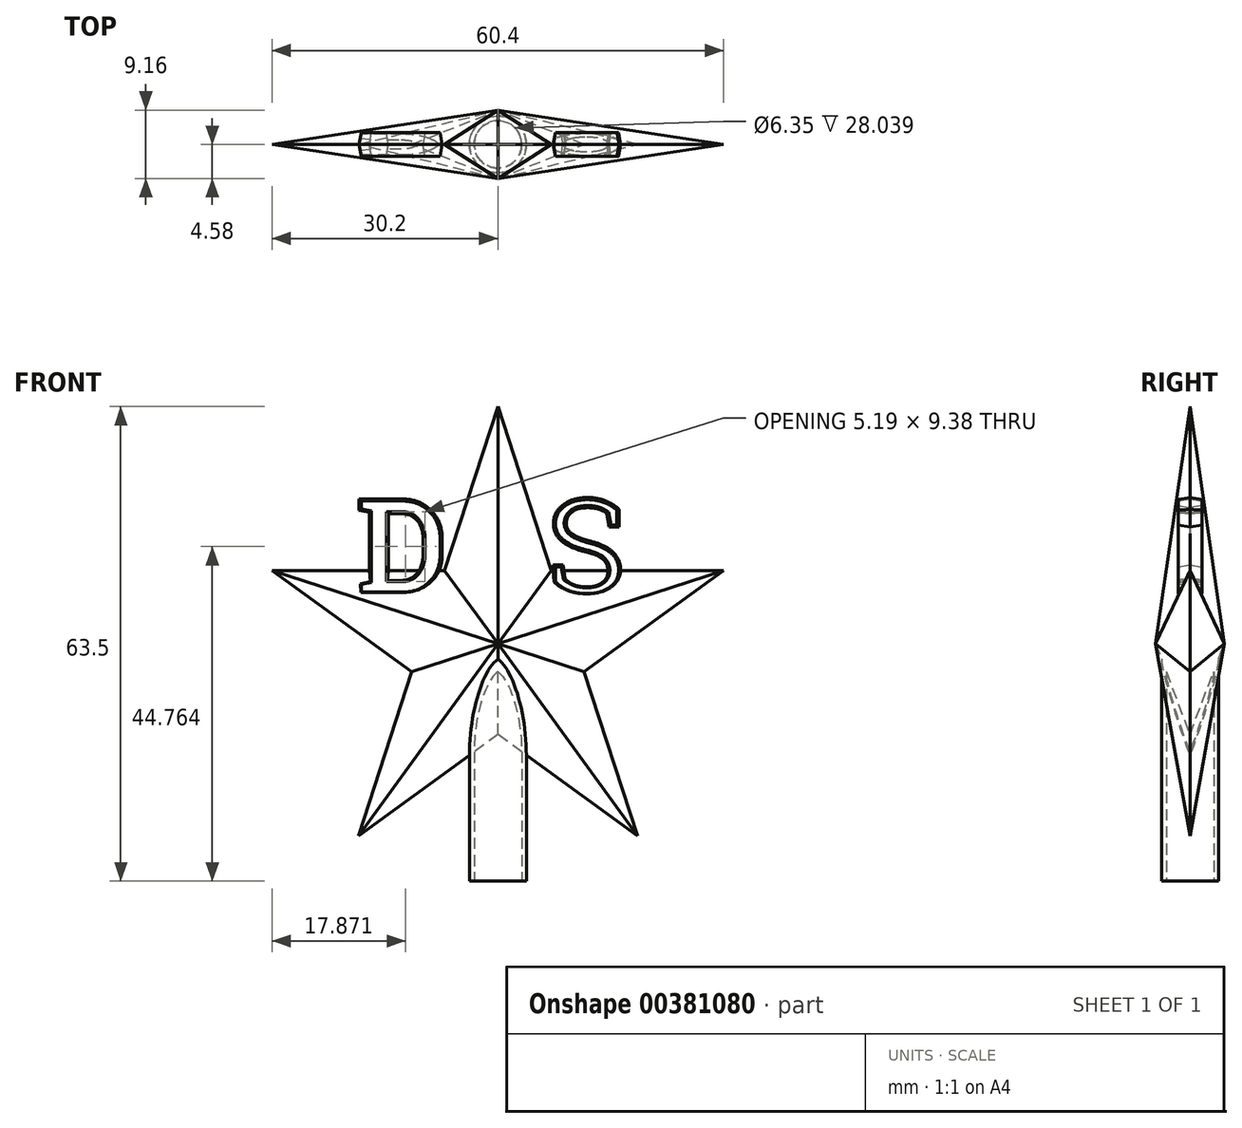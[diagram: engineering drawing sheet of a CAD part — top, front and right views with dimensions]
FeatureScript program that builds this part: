
annotation { "Feature Type Name" : "Feature", "Feature Type Description" : "" }
export const myFeature = defineFeature(function(context is Context, id is Id, definition is map)
    precondition{}
    {
        {
            var Q0;
            Q0=qCreatedBy(makeId("Front.planeOp"),FACE);
            var sketch = newSketch(context, id + "F0", { "sketchPlane" : qUnion([Q0])});
            skCircle(sketch, "E0", {"center": v(0, 31.75) * mm, "radius": 31.75 * mm, "construction": true});
            skPoint(sketch, "E1", {"position": v(0, 63.5) * mm});
            skPoint(sketch, "E2", {"position": v(30.2, 41.56) * mm});
            skPoint(sketch, "E3", {"position": v(18.66, 6.06) * mm});
            skPoint(sketch, "E4", {"position": v(-18.66, 6.06) * mm});
            skPoint(sketch, "E5", {"position": v(-30.2, 41.56) * mm});
            skLineSegment(sketch, "E6", {"start": v(0, 63.5) * mm, "end": v(7.13, 41.56) * mm});
            skLineSegment(sketch, "E7", {"start": v(7.13, 41.56) * mm, "end": v(30.2, 41.56) * mm});
            skLineSegment(sketch, "E8", {"start": v(30.2, 41.56) * mm, "end": v(11.53, 28) * mm});
            skLineSegment(sketch, "E9", {"start": v(11.53, 28) * mm, "end": v(18.66, 6.06) * mm});
            skLineSegment(sketch, "E10", {"start": v(18.66, 6.06) * mm, "end": v(0, 19.62) * mm});
            skLineSegment(sketch, "E11", {"start": v(0, 19.62) * mm, "end": v(-18.66, 6.06) * mm});
            skLineSegment(sketch, "E12", {"start": v(-18.66, 6.06) * mm, "end": v(-11.53, 28) * mm});
            skLineSegment(sketch, "E13", {"start": v(-11.53, 28) * mm, "end": v(-30.2, 41.56) * mm});
            skLineSegment(sketch, "E14", {"start": v(-30.2, 41.56) * mm, "end": v(-7.13, 41.56) * mm});
            skLineSegment(sketch, "E15", {"start": v(-7.13, 41.56) * mm, "end": v(0, 63.5) * mm});
            skCircle(sketch, "E16", {"center": v(0, 31.75) * mm, "radius": 12.13 * mm, "construction": true});
            skSolve(sketch);
        }
        {
            var Q0;
            Q0 = qSketchRegion(id + "F0", true);
            var Q1;
            Q1=sQuery(id+"F0.wireOp",EDGE,"E15");
            var Q2;
            Q2=sQuery(id+"F0.wireOp",EDGE,"E6");
            var Q3;
            Q3=sQuery(id+"F0.wireOp",EDGE,"E7");
            var Q4;
            Q4=sQuery(id+"F0.wireOp",EDGE,"E8");
            var Q5;
            Q5=sQuery(id+"F0.wireOp",EDGE,"E9");
            var Q6;
            Q6=sQuery(id+"F0.wireOp",EDGE,"E14");
            var Q7;
            Q7=sQuery(id+"F0.wireOp",EDGE,"E13");
            var Q8;
            Q8=sQuery(id+"F0.wireOp",EDGE,"E12");
            var Q9;
            Q9=sQuery(id+"F0.wireOp",EDGE,"E11");
            var Q10;
            Q10=sQuery(id+"F0.wireOp",EDGE,"E10");
            extrude(context, id + "F1", {"entities" : qUnion([Q0]), "surfaceEntities" : qUnion([Q1, Q2, Q3, Q4, Q5, Q6, Q7, Q8, Q9, Q10]), "endBound" : BoundingType.SYMMETRIC, "depth" : 19.05 * mm, "hasDraft" : true, "draftAngle" : 65 * degree, "draftPullDirection" : true});
        }
        {
            var Q0;
            Q0=qCreatedBy(makeId("Top.planeOp"),FACE);
            var sketch = newSketch(context, id + "F2", { "sketchPlane" : qUnion([Q0])});
            skCircle(sketch, "E17", {"center": v(0, 0) * mm, "radius": 3.81 * mm});
            skCircle(sketch, "E18", {"center": v(0, 0) * mm, "radius": 3.18 * mm});
            skSolve(sketch);
        }
        {
            var Q0;
            Q0 = qSketchRegion(id + "F2", true);
            extrude(context, id + "F3", {"entities" : qUnion([Q0]), "operationType" : NewBodyOperationType.ADD, "depth" : 31.75 * mm});
        }
        {
            var Q0;
            Q0=qCreatedBy(makeId("Front.planeOp"),FACE);
            var sketch = newSketch(context, id + "F4", { "sketchPlane" : qUnion([Q0])});
            skText(sketch, "E19", { "text": "D", "fontName": "RobotoSlab-Bold.ttf"});
            skText(sketch, "E20", { "text": "S", "fontName": "RobotoSlab-Regular.ttf"});
            const initialGuessF4  = {"E19": [-0.01905, 0.03839, 1, 0, 0.01292], "E20": [0.00635, 0.03839, 1, 0, 0.01292]};
            skSetInitialGuess(sketch, initialGuessF4);
            skSolve(sketch);
        }
        {
            var Q0;
            Q0 = qSketchRegion(id + "F4", true);
            extrude(context, id + "F5", {"entities" : qUnion([Q0]), "operationType" : NewBodyOperationType.ADD, "endBound" : BoundingType.SYMMETRIC, "depth" : 3.17 * mm, "hasDraft" : true, "draftAngle" : 10 * degree, "draftPullDirection" : true});
        }
    });
